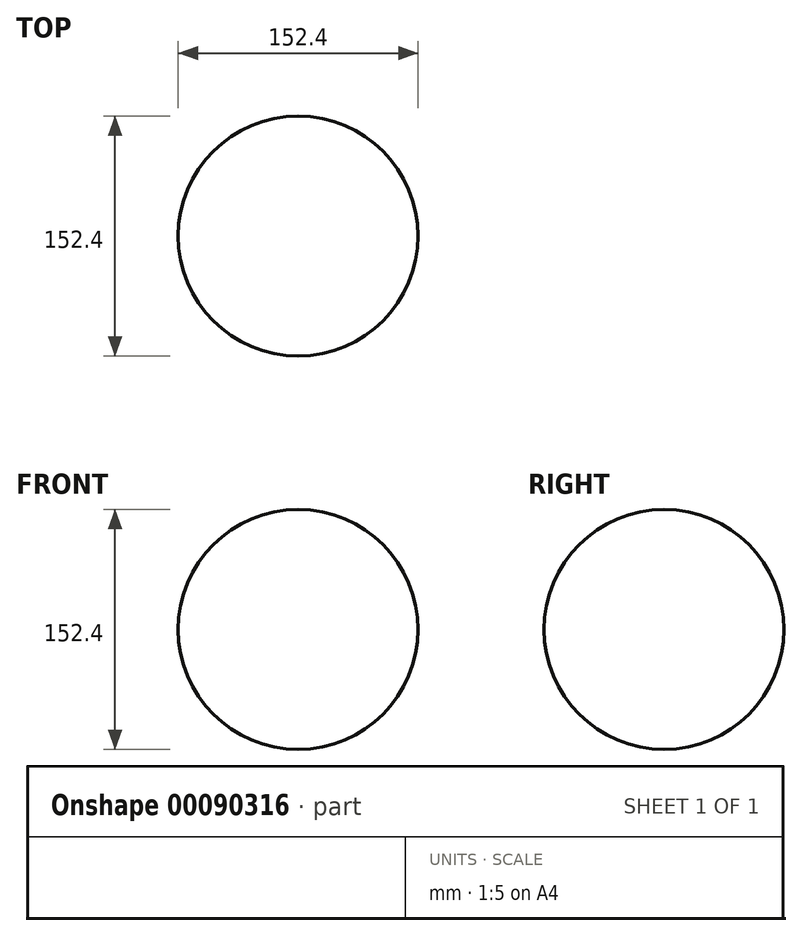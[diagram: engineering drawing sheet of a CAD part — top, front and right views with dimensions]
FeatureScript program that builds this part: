
annotation { "Feature Type Name" : "Feature", "Feature Type Description" : "" }
export const myFeature = defineFeature(function(context is Context, id is Id, definition is map)
    precondition{}
    {
        {
            var Q0;
            Q0=qCreatedBy(makeId("Front.planeOp"),FACE);
            var sketch = newSketch(context, id + "F0", { "sketchPlane" : qUnion([Q0])});
            skCircle(sketch, "E0", {"center": v(0, 0) * mm, "radius": 76.2 * mm});
            skLineSegment(sketch, "E1", {"start": v(0, 76.2) * mm, "end": v(0, -76.2) * mm});
            skSolve(sketch);
        }
        {
            var Q0;
            {var subQ0=sQuery(id+"F0.wireOp",EDGE,"E1");Q0=makeQuery(id+"F0.imprint","IMPRINT",FACE,{"disambiguationData":[TD([[makeQuery(id+"F0.imprint","IMPRINT",EDGE,{"derivedFrom":subQ0}),-1.0]])]});}
            var Q1;
            Q1=sQuery(id+"F0.wireOp",EDGE,"E1");
            revolve(context, id + "F1", {"entities" : qUnion([Q0]), "axis" : qUnion([Q1]), "revolveType" : RevolveType.FULL});
        }
    });
